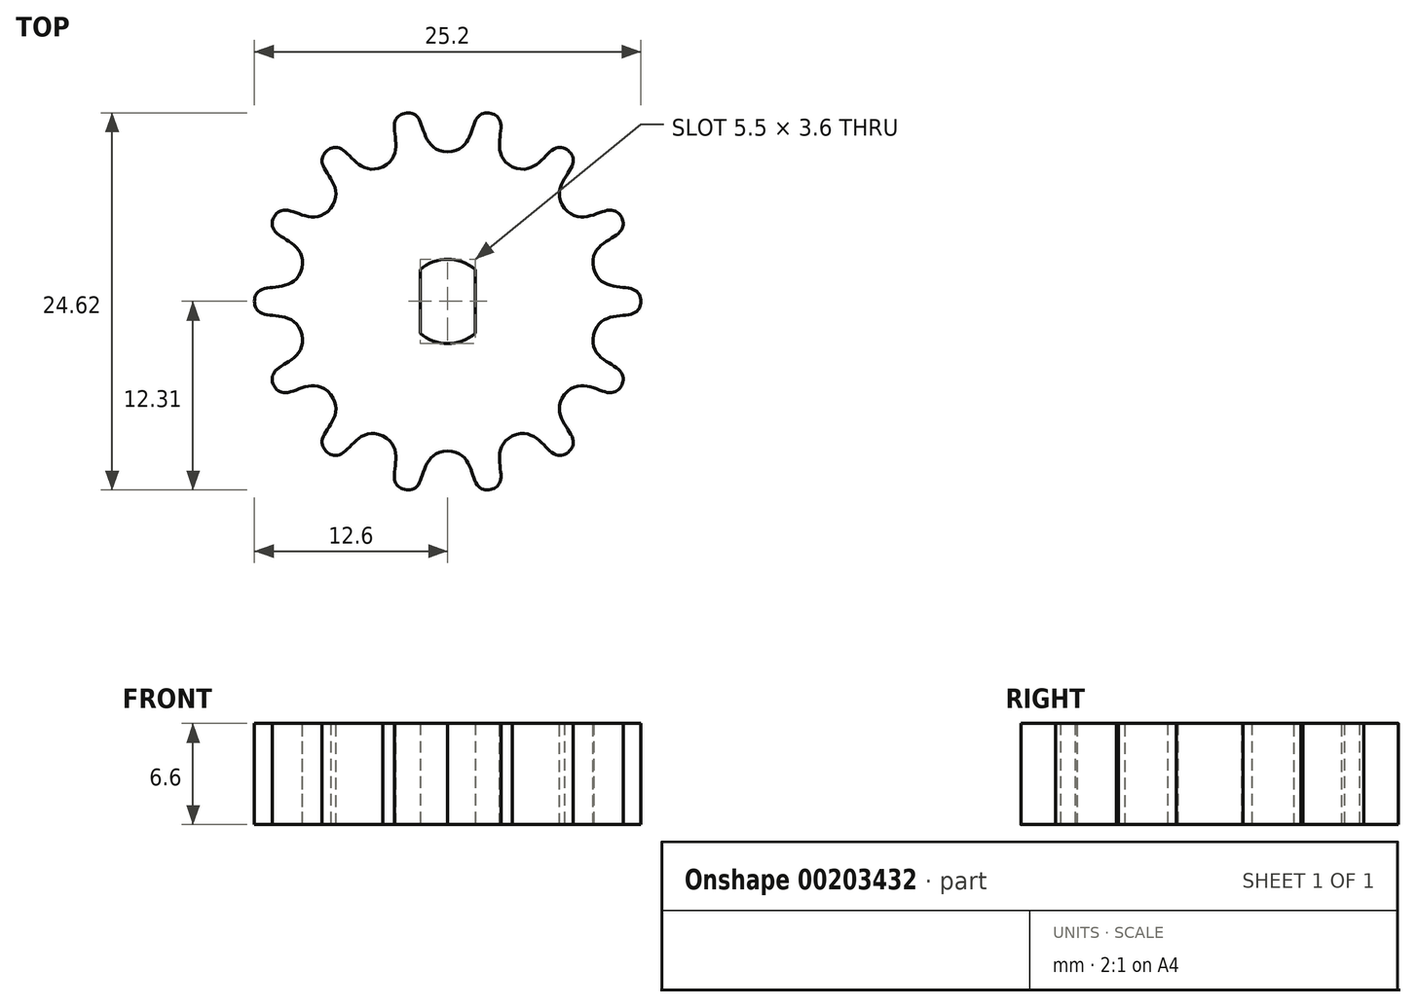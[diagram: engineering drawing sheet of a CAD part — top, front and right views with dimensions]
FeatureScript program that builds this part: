
annotation { "Feature Type Name" : "Feature", "Feature Type Description" : "" }
export const myFeature = defineFeature(function(context is Context, id is Id, definition is map)
    precondition{}
    {
        {
            assignVariable(context, id + "F0", {"name" : "teeth", "anyValue" : 14});
        }
        {
            assignVariable(context, id + "F1", {"name" : "gear_thickness", "anyValue" : 6.6});
        }
        {
            var Q0;
            Q0=qCreatedBy(makeId("Top.planeOp"),FACE);
            var sketch = newSketch(context, id + "F2", { "sketchPlane" : qUnion([Q0])});
            skCircle(sketch, "E0", {"center": v(0, 0) * mm, "radius": 12.6 * mm});
            skCircle(sketch, "E1", {"center": v(0, 0) * mm, "radius": 9.75 * mm});
            skCircle(sketch, "E2", {"center": v(0, 0) * mm, "radius": 2.75 * mm});
            skLineSegment(sketch, "E3.bottom", {"start": v(-1.8, 2.08) * mm, "end": v(1.8, 2.08) * mm});
            skLineSegment(sketch, "E3.top", {"start": v(-1.8, -2.08) * mm, "end": v(1.8, -2.08) * mm});
            skLineSegment(sketch, "E3.left", {"start": v(-1.8, 2.08) * mm, "end": v(-1.8, -2.08) * mm});
            skLineSegment(sketch, "E3.right", {"start": v(1.8, 2.08) * mm, "end": v(1.8, -2.08) * mm});
            skPoint(sketch, "E4", {"position": v(0, 9.75) * mm});
            skLineSegment(sketch, "E5", {"start": v(0, 0) * mm, "end": v(0, 15.09) * mm});
            skLineSegment(sketch, "E6", {"start": v(0, 0) * mm, "end": v(6.63, 13.76) * mm});
            skLineSegment(sketch, "E7", {"start": v(0, 0) * mm, "end": v(3.32, 14.54) * mm});
            skFitSpline(sketch, "E8", {"points": [v(0, 9.75) * mm, v(1.88, 11.9) * mm, v(2.8, 12.28) * mm, v(3.47, 11.54) * mm, v(4.23, 8.78) * mm], "startDerivative": vector(14.37, 0.54) * mm, "endDerivative": vector(12.71, -6.72) * mm});
            skSolve(sketch);
        }
        {
            var Q0;
            {var subQ1=sQuery(id+"F2.wireOp",EDGE,"E1");var subQ3=sQuery(id+"F2.wireOp",EDGE,"E7");var subQ4=makeQuery(id+"F2.imprint","INTERSECT",VERTEX,{"derivedFrom":[subQ1,subQ3]});Q0=makeQuery(id+"F2.imprint","IMPRINT",FACE,{"disambiguationData":[TD([[makeQuery(id+"F2.imprint","IMPRINT",EDGE,{"disambiguationData":[TD([[subQ4,-1.0]])],"derivedFrom":subQ1}),-1.0]])]});}
            var Q1;
            {var subQ1=sQuery(id+"F2.wireOp",EDGE,"E1");var subQ3=sQuery(id+"F2.wireOp",EDGE,"E7");var subQ4=makeQuery(id+"F2.imprint","INTERSECT",VERTEX,{"derivedFrom":[subQ1,subQ3]});Q1=makeQuery(id+"F2.imprint","IMPRINT",FACE,{"disambiguationData":[TD([[makeQuery(id+"F2.imprint","IMPRINT",EDGE,{"disambiguationData":[TD([[subQ4,1.0]])],"derivedFrom":subQ1}),-1.0]])]});}
            var Q2;
            {var subQ3=sQuery(id+"F2.wireOp",EDGE,"E7");var subQ5=sQuery(id+"F2.wireOp",EDGE,"E2");var subQ7=makeQuery(id+"F2.imprint","INTERSECT",VERTEX,{"derivedFrom":[subQ5,subQ3]});Q2=makeQuery(id+"F2.imprint","IMPRINT",FACE,{"disambiguationData":[TD([[makeQuery(id+"F2.imprint","IMPRINT",EDGE,{"disambiguationData":[TD([[subQ7,-1.0]])],"derivedFrom":subQ5}),-1.0]])]});}
            var Q3;
            {var subQ0=sQuery(id+"F2.wireOp",EDGE,"E6");var subQ5=sQuery(id+"F2.wireOp",EDGE,"E2");var subQ6=makeQuery(id+"F2.imprint","INTERSECT",VERTEX,{"derivedFrom":[subQ5,subQ0]});Q3=makeQuery(id+"F2.imprint","IMPRINT",FACE,{"disambiguationData":[TD([[makeQuery(id+"F2.imprint","IMPRINT",EDGE,{"disambiguationData":[TD([[subQ6,-1.0]])],"derivedFrom":subQ5}),-1.0]])]});}
            var Q4;
            {var subQ0=sQuery(id+"F2.wireOp",EDGE,"E7");var subQ1=sQuery(id+"F2.wireOp",EDGE,"E2");var subQ2=makeQuery(id+"F2.imprint","INTERSECT",VERTEX,{"derivedFrom":[subQ1,subQ0]});Q4=makeQuery(id+"F2.imprint","IMPRINT",FACE,{"disambiguationData":[TD([[makeQuery(id+"F2.imprint","IMPRINT",EDGE,{"disambiguationData":[TD([[subQ2,-1.0]])],"derivedFrom":subQ1}),1.0]])]});}
            var Q5;
            {var subQ0=sQuery(id+"F2.wireOp",EDGE,"E6");var subQ1=sQuery(id+"F2.wireOp",EDGE,"E2");var subQ2=makeQuery(id+"F2.imprint","INTERSECT",VERTEX,{"derivedFrom":[subQ1,subQ0]});Q5=makeQuery(id+"F2.imprint","IMPRINT",FACE,{"disambiguationData":[TD([[makeQuery(id+"F2.imprint","IMPRINT",EDGE,{"disambiguationData":[TD([[subQ2,-1.0]])],"derivedFrom":subQ1}),1.0]])]});}
            var Q6;
            {var subQ0=sQuery(id+"F2.wireOp",EDGE,"E5");var subQ1=sQuery(id+"F2.wireOp",EDGE,"E3.bottom");var subQ2=makeQuery(id+"F2.imprint","INTERSECT",VERTEX,{"derivedFrom":[subQ1,subQ0]});Q6=makeQuery(id+"F2.imprint","IMPRINT",FACE,{"disambiguationData":[TD([[makeQuery(id+"F2.imprint","IMPRINT",EDGE,{"disambiguationData":[TD([[subQ2,-1.0]])],"derivedFrom":subQ1}),-1.0]])]});}
            var Q7;
            {var subQ0=sQuery(id+"F2.wireOp",EDGE,"E7");var subQ1=sQuery(id+"F2.wireOp",EDGE,"E3.bottom");var subQ2=makeQuery(id+"F2.imprint","INTERSECT",VERTEX,{"derivedFrom":[subQ1,subQ0]});Q7=makeQuery(id+"F2.imprint","IMPRINT",FACE,{"disambiguationData":[TD([[makeQuery(id+"F2.imprint","IMPRINT",EDGE,{"disambiguationData":[TD([[subQ2,-1.0]])],"derivedFrom":subQ1}),-1.0]])]});}
            extrude(context, id + "F3", {"entities" : qUnion([Q0, Q1, Q2, Q3, Q4, Q5, Q6, Q7]), "depth" : (getVariable(context, 'gear_thickness')) * mm});
        }
        {
            var Q0;
            Q0=makeQuery(id+"F3.opExtrude","SWEPT_BODY",BODY,{"disambiguationData":[OSD([sQuery(id+"F2.wireOp",EDGE,"E5"),sQuery(id+"F2.wireOp",EDGE,"E6"),sQuery(id+"F2.wireOp",EDGE,"E8")])]});
            var Q1;
            Q1=makeQuery(id+"F3.opExtrude","SWEPT_EDGE",EDGE,{"disambiguationData":[OSD([sQuery(id+"F2.wireOp",EDGE,"E5"),sQuery(id+"F2.wireOp",EDGE,"E6"),sQuery(id+"F2.wireOp",EDGE,"E7")])]});
            circularPattern(context, id + "F4", {"operationType" : NewBodyOperationType.ADD, "entities" : qUnion([Q0]), "axis" : qUnion([Q1]), "angle" : 360 * degree, "instanceCount" : getVariable(context, 'teeth'), "equalSpace" : true});
        }
        {
            var Q0;
            Q0=makeQuery(id+"F2.imprint","IMPRINT",FACE,{"disambiguationData":[TD([[makeQuery(id+"F2.imprint","IMPRINT",EDGE,{"derivedFrom":sQuery(id+"F2.wireOp",EDGE,"E3.top")}),1.0]])]});
            var Q1;
            {var subQ0=sQuery(id+"F2.wireOp",EDGE,"E3.top");Q1=makeQuery(id+"F2.imprint","IMPRINT",FACE,{"disambiguationData":[TD([[makeQuery(id+"F2.imprint","IMPRINT",EDGE,{"derivedFrom":subQ0}),-1.0]])]});}
            var Q2;
            {var subQ1=sQuery(id+"F2.wireOp",EDGE,"E2");var subQ3=sQuery(id+"F2.wireOp",EDGE,"E5");var subQ4=makeQuery(id+"F2.imprint","INTERSECT",VERTEX,{"derivedFrom":[subQ1,subQ3]});Q2=makeQuery(id+"F2.imprint","IMPRINT",FACE,{"disambiguationData":[TD([[makeQuery(id+"F2.imprint","IMPRINT",EDGE,{"disambiguationData":[TD([[subQ4,1.0]])],"derivedFrom":subQ3}),1.0]])]});}
            var Q3;
            {var subQ0=sQuery(id+"F2.wireOp",EDGE,"E7");var subQ1=sQuery(id+"F2.wireOp",EDGE,"E2");var subQ2=makeQuery(id+"F2.imprint","INTERSECT",VERTEX,{"derivedFrom":[subQ1,subQ0]});Q3=makeQuery(id+"F2.imprint","IMPRINT",FACE,{"disambiguationData":[TD([[makeQuery(id+"F2.imprint","IMPRINT",EDGE,{"disambiguationData":[TD([[subQ2,-1.0]])],"derivedFrom":subQ1}),1.0]])]});}
            var Q4;
            {var subQ0=sQuery(id+"F2.wireOp",EDGE,"E6");var subQ1=sQuery(id+"F2.wireOp",EDGE,"E2");var subQ2=makeQuery(id+"F2.imprint","INTERSECT",VERTEX,{"derivedFrom":[subQ1,subQ0]});Q4=makeQuery(id+"F2.imprint","IMPRINT",FACE,{"disambiguationData":[TD([[makeQuery(id+"F2.imprint","IMPRINT",EDGE,{"disambiguationData":[TD([[subQ2,-1.0]])],"derivedFrom":subQ1}),1.0]])]});}
            var Q5;
            {var subQ1=sQuery(id+"F2.wireOp",EDGE,"E2");var subQ3=sQuery(id+"F2.wireOp",EDGE,"E6");var subQ4=makeQuery(id+"F2.imprint","INTERSECT",VERTEX,{"derivedFrom":[subQ1,subQ3]});Q5=makeQuery(id+"F2.imprint","IMPRINT",FACE,{"disambiguationData":[TD([[makeQuery(id+"F2.imprint","IMPRINT",EDGE,{"disambiguationData":[TD([[subQ4,1.0]])],"derivedFrom":subQ3}),-1.0]])]});}
            var Q6;
            {var subQ0=sQuery(id+"F2.wireOp",EDGE,"E7");var subQ1=sQuery(id+"F2.wireOp",EDGE,"E3.bottom");var subQ2=makeQuery(id+"F2.imprint","INTERSECT",VERTEX,{"derivedFrom":[subQ1,subQ0]});Q6=makeQuery(id+"F2.imprint","IMPRINT",FACE,{"disambiguationData":[TD([[makeQuery(id+"F2.imprint","IMPRINT",EDGE,{"disambiguationData":[TD([[subQ2,-1.0]])],"derivedFrom":subQ1}),-1.0]])]});}
            var Q7;
            {var subQ0=sQuery(id+"F2.wireOp",EDGE,"E5");var subQ1=sQuery(id+"F2.wireOp",EDGE,"E3.bottom");var subQ2=makeQuery(id+"F2.imprint","INTERSECT",VERTEX,{"derivedFrom":[subQ1,subQ0]});Q7=makeQuery(id+"F2.imprint","IMPRINT",FACE,{"disambiguationData":[TD([[makeQuery(id+"F2.imprint","IMPRINT",EDGE,{"disambiguationData":[TD([[subQ2,-1.0]])],"derivedFrom":subQ1}),-1.0]])]});}
            extrude(context, id + "F5", {"entities" : qUnion([Q0, Q1, Q2, Q3, Q4, Q5, Q6, Q7]), "operationType" : NewBodyOperationType.REMOVE, "endBound" : BoundingType.THROUGH_ALL, "depth" : 25 * mm});
        }
    });
